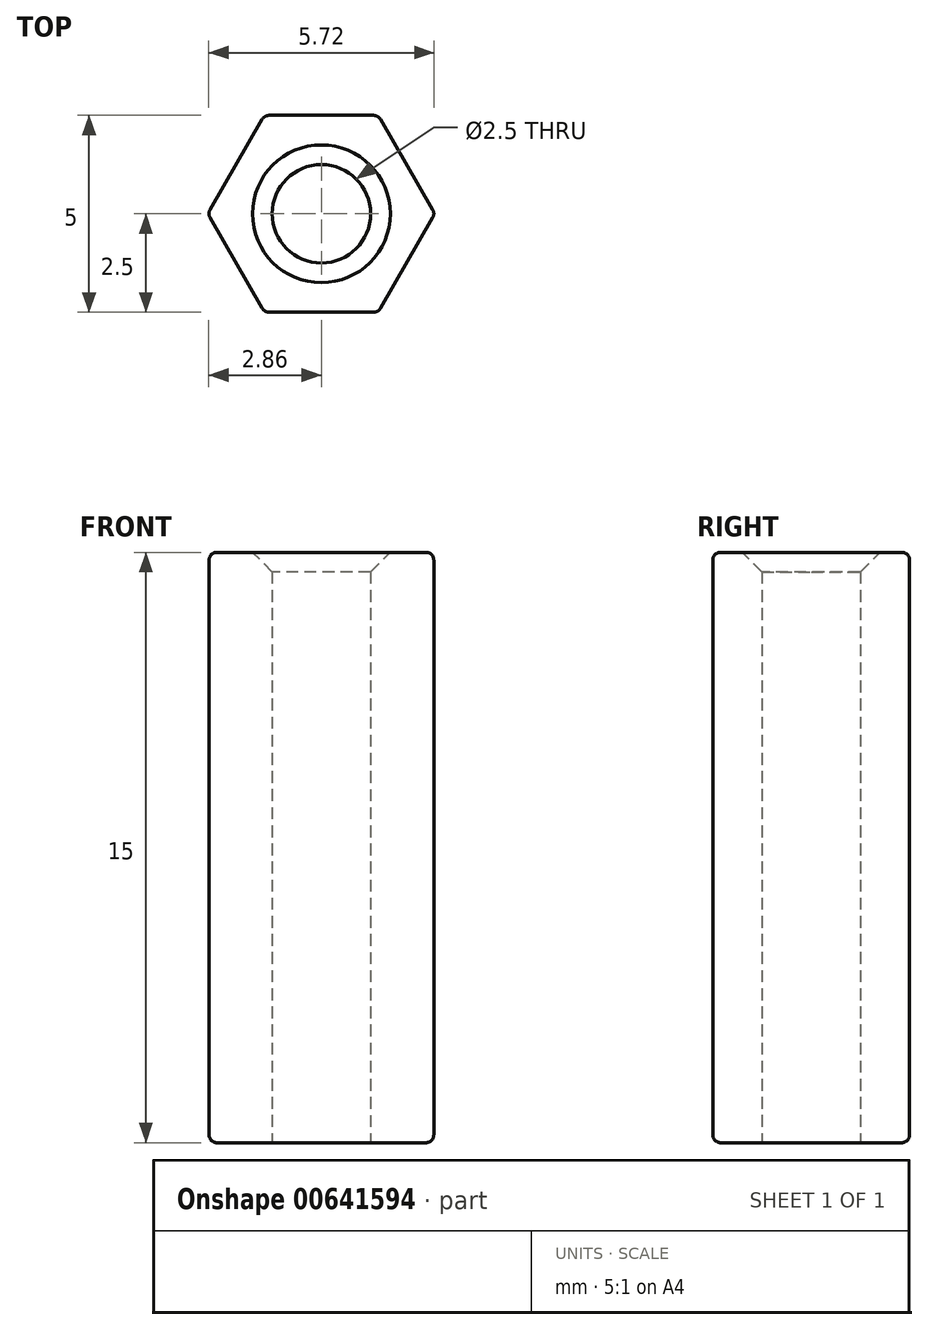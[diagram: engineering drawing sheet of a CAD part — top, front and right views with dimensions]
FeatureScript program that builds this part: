
annotation { "Feature Type Name" : "Feature", "Feature Type Description" : "" }
export const myFeature = defineFeature(function(context is Context, id is Id, definition is map)
    precondition{}
    {
        {
            var Q0;
            Q0=qCreatedBy(makeId("Top.planeOp"),FACE);
            var sketch = newSketch(context, id + "F0", { "sketchPlane" : qUnion([Q0])});
            skCircle(sketch, "E0.cCircle", {"center": v(0, 0) * mm, "radius": 2.5 * mm, "construction": true});
            skLineSegment(sketch, "E0.0", {"start": v(-1.44, 2.5) * mm, "end": v(1.44, 2.5) * mm});
            skLineSegment(sketch, "E0.1", {"start": v(1.44, 2.5) * mm, "end": v(2.89, 0) * mm});
            skLineSegment(sketch, "E0.2", {"start": v(2.89, 0) * mm, "end": v(1.44, -2.5) * mm});
            skLineSegment(sketch, "E0.3", {"start": v(1.44, -2.5) * mm, "end": v(-1.44, -2.5) * mm});
            skLineSegment(sketch, "E0.4", {"start": v(-1.44, -2.5) * mm, "end": v(-2.89, 0) * mm});
            skLineSegment(sketch, "E0.5", {"start": v(-2.89, 0) * mm, "end": v(-1.44, 2.5) * mm});
            skPoint(sketch, "E0.0.midPoint", {"position": v(0, 2.5) * mm});
            skCircle(sketch, "E1", {"center": v(0, 0) * mm, "radius": 1.25 * mm});
            skSolve(sketch);
        }
        {
            var Q0;
            Q0 = qSketchRegion(id + "F0", true);
            extrude(context, id + "F1", {"entities" : qUnion([Q0]), "depth" : 15 * mm, "offsetDistance" : 25 * mm});
        }
        {
            var Q0;
            Q0=makeQuery(id+"F1.opExtrude","CAP_EDGE",EDGE,{"disambiguationData":[OSD([sQuery(id+"F0.wireOp",EDGE,"E1")])],"isStart":false});
            chamfer(context, id + "F2", {"entities" : qUnion([Q0]), "width" : 0.5 * mm, "tangentPropagation" : true});
        }
        {
            var Q0;
            Q0=makeQuery(id+"F1.opExtrude","CAP_EDGE",EDGE,{"disambiguationData":[OSD([sQuery(id+"F0.wireOp",EDGE,"E0.4")])],"isStart":false});
            var Q1;
            Q1=makeQuery(id+"F1.opExtrude","CAP_EDGE",EDGE,{"disambiguationData":[OSD([sQuery(id+"F0.wireOp",EDGE,"E0.3")])],"isStart":false});
            var Q2;
            Q2=makeQuery(id+"F1.opExtrude","CAP_EDGE",EDGE,{"disambiguationData":[OSD([sQuery(id+"F0.wireOp",EDGE,"E0.2")])],"isStart":false});
            var Q3;
            Q3=makeQuery(id+"F1.opExtrude","CAP_EDGE",EDGE,{"disambiguationData":[OSD([sQuery(id+"F0.wireOp",EDGE,"E0.1")])],"isStart":false});
            var Q4;
            Q4=makeQuery(id+"F1.opExtrude","CAP_EDGE",EDGE,{"disambiguationData":[OSD([sQuery(id+"F0.wireOp",EDGE,"E0.0")])],"isStart":false});
            var Q5;
            Q5=makeQuery(id+"F1.opExtrude","CAP_EDGE",EDGE,{"disambiguationData":[OSD([sQuery(id+"F0.wireOp",EDGE,"E0.5")])],"isStart":false});
            var Q6;
            Q6=makeQuery(id+"F1.opExtrude","CAP_EDGE",EDGE,{"disambiguationData":[OSD([sQuery(id+"F0.wireOp",EDGE,"E0.4")])],"isStart":true});
            var Q7;
            Q7=makeQuery(id+"F1.opExtrude","CAP_EDGE",EDGE,{"disambiguationData":[OSD([sQuery(id+"F0.wireOp",EDGE,"E0.3")])],"isStart":true});
            var Q8;
            Q8=makeQuery(id+"F1.opExtrude","CAP_EDGE",EDGE,{"disambiguationData":[OSD([sQuery(id+"F0.wireOp",EDGE,"E0.2")])],"isStart":true});
            var Q9;
            Q9=makeQuery(id+"F1.opExtrude","CAP_EDGE",EDGE,{"disambiguationData":[OSD([sQuery(id+"F0.wireOp",EDGE,"E0.1")])],"isStart":true});
            var Q10;
            Q10=makeQuery(id+"F1.opExtrude","CAP_EDGE",EDGE,{"disambiguationData":[OSD([sQuery(id+"F0.wireOp",EDGE,"E0.0")])],"isStart":true});
            var Q11;
            Q11=makeQuery(id+"F1.opExtrude","CAP_EDGE",EDGE,{"disambiguationData":[OSD([sQuery(id+"F0.wireOp",EDGE,"E0.5")])],"isStart":true});
            var Q12;
            Q12=makeQuery(id+"F1.opExtrude","SWEPT_EDGE",EDGE,{"disambiguationData":[OSD([sQuery(id+"F0.wireOp",EDGE,"E0.3"),sQuery(id+"F0.wireOp",EDGE,"E0.4")])]});
            var Q13;
            Q13=makeQuery(id+"F1.opExtrude","SWEPT_EDGE",EDGE,{"disambiguationData":[OSD([sQuery(id+"F0.wireOp",EDGE,"E0.2"),sQuery(id+"F0.wireOp",EDGE,"E0.3")])]});
            var Q14;
            Q14=makeQuery(id+"F1.opExtrude","SWEPT_EDGE",EDGE,{"disambiguationData":[OSD([sQuery(id+"F0.wireOp",EDGE,"E0.4"),sQuery(id+"F0.wireOp",EDGE,"E0.5")])]});
            var Q15;
            Q15=makeQuery(id+"F1.opExtrude","SWEPT_EDGE",EDGE,{"disambiguationData":[OSD([sQuery(id+"F0.wireOp",EDGE,"E0.0"),sQuery(id+"F0.wireOp",EDGE,"E0.5")])]});
            var Q16;
            Q16=makeQuery(id+"F1.opExtrude","SWEPT_EDGE",EDGE,{"disambiguationData":[OSD([sQuery(id+"F0.wireOp",EDGE,"E0.0"),sQuery(id+"F0.wireOp",EDGE,"E0.1")])]});
            var Q17;
            Q17=makeQuery(id+"F1.opExtrude","SWEPT_EDGE",EDGE,{"disambiguationData":[OSD([sQuery(id+"F0.wireOp",EDGE,"E0.1"),sQuery(id+"F0.wireOp",EDGE,"E0.2")])]});
            fillet(context, id + "F3", {"entities" : qUnion([Q0, Q1, Q2, Q3, Q4, Q5, Q6, Q7, Q8, Q9, Q10, Q11, Q12, Q13, Q14, Q15, Q16, Q17]), "radius" : 0.2 * mm, "tangentPropagation" : true, "allowEdgeOverflow" : false});
        }
    });
